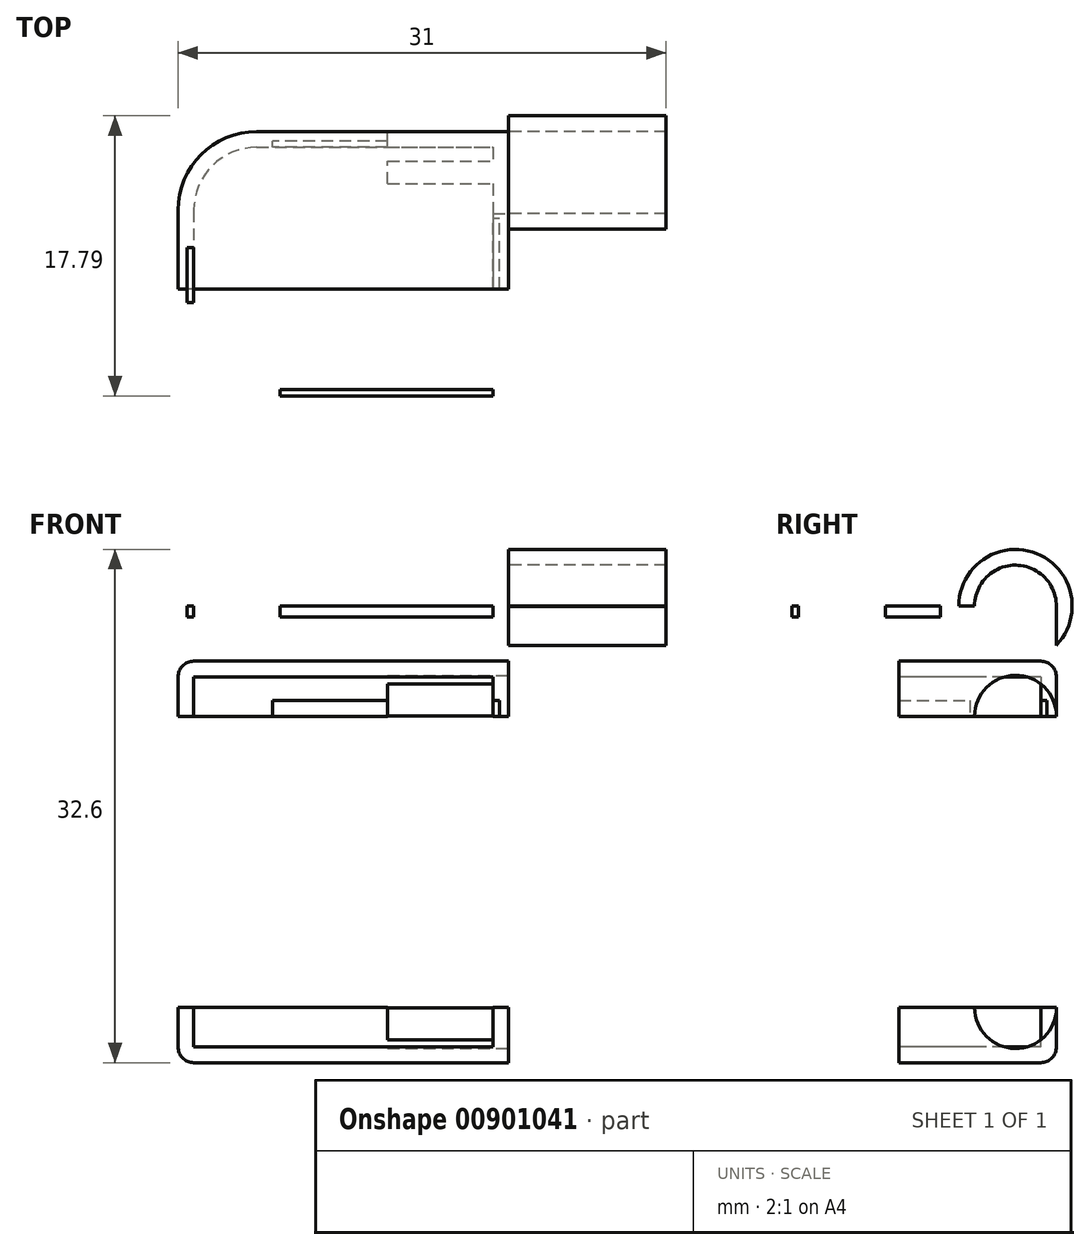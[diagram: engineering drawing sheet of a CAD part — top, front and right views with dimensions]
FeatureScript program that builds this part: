
annotation { "Feature Type Name" : "Feature", "Feature Type Description" : "" }
export const myFeature = defineFeature(function(context is Context, id is Id, definition is map)
    precondition{}
    {
        {
            var Q0;
            Q0=qCreatedBy(makeId("Top.planeOp"),FACE);
            var sketch = newSketch(context, id + "F0", { "sketchPlane" : qUnion([Q0])});
            skLineSegment(sketch, "E0.bottom", {"start": v(-4.03, 8.7) * mm, "end": v(11.97, 8.7) * mm});
            skLineSegment(sketch, "E0.top", {"start": v(-9.03, -1.3) * mm, "end": v(11.97, -1.3) * mm});
            skLineSegment(sketch, "E0.left", {"start": v(-9.03, 3.7) * mm, "end": v(-9.03, -1.3) * mm});
            skLineSegment(sketch, "E0.right", {"start": v(11.97, 8.7) * mm, "end": v(11.97, -1.3) * mm});
            skPoint(sketch, "E1.visualSharp", {"position": v(-9.03, 8.7) * mm});
            skArc(sketch, "E1.filletArc", {"start": v(-4.03, 8.7) * mm, "mid": v(-7.56, 7.23) * mm, "end": v(-9.03, 3.7) * mm});
            skSolve(sketch);
        }
        {
            var Q0;
            Q0=qSketchRegion(id+"F0",true);
            extrude(context, id + "F1", {"entities" : qUnion([Q0]), "depth" : 3.5 * mm, "offsetDistance" : 25 * mm});
        }
        {
            var Q0;
            Q0=makeQuery(id+"F1.opExtrude","CAP_FACE",FACE,{"disambiguationData":[OSD([sQuery(id+"F0.wireOp",EDGE,"E0.bottom"),sQuery(id+"F0.wireOp",EDGE,"E0.top"),sQuery(id+"F0.wireOp",EDGE,"E0.left"),sQuery(id+"F0.wireOp",EDGE,"E0.right"),sQuery(id+"F0.wireOp",EDGE,"E1.filletArc")])],"isStart":false});
            var sketch = newSketch(context, id + "F2", { "sketchPlane" : qUnion([Q0])});
            skLineSegment(sketch, "E2.0", {"start": v(-8.03, 3.7) * mm, "end": v(-8.03, -1.3) * mm});
            skArc(sketch, "E2.1", {"start": v(-4.03, 7.7) * mm, "mid": v(-6.86, 6.52) * mm, "end": v(-8.03, 3.7) * mm});
            skLineSegment(sketch, "E2.2", {"start": v(-4.03, 7.7) * mm, "end": v(10.97, 7.7) * mm});
            skLineSegment(sketch, "E2.3", {"start": v(10.97, 7.7) * mm, "end": v(10.97, -1.3) * mm});
            skSolve(sketch);
        }
        {
            var Q0;
            {var subQ1=sQuery(id+"F2.wireOp",EDGE,"E2.0");Q0=makeQuery(id+"F2.imprint","IMPRINT",FACE,{"disambiguationData":[TD([[makeQuery(id+"F2.imprint","IMPRINT",EDGE,{"derivedFrom":subQ1}),1.0]])]});}
            extrude(context, id + "F3", {"entities" : qUnion([Q0]), "operationType" : NewBodyOperationType.REMOVE, "oppositeDirection" : true, "depth" : 2.5 * mm, "offsetDistance" : 25 * mm});
        }
        {
            var Q0;
            Q0=makeQuery(id+"F1.opExtrude","CAP_EDGE",EDGE,{"disambiguationData":[OSD([sQuery(id+"F0.wireOp",EDGE,"E0.bottom")])],"isStart":true});
            var Q1;
            Q1=makeQuery(id+"F1.opExtrude","CAP_EDGE",EDGE,{"disambiguationData":[OSD([sQuery(id+"F0.wireOp",EDGE,"E1.filletArc")])],"isStart":true});
            var Q2;
            Q2=makeQuery(id+"F1.opExtrude","CAP_EDGE",EDGE,{"disambiguationData":[OSD([sQuery(id+"F0.wireOp",EDGE,"E0.left")])],"isStart":true});
            fillet(context, id + "F4", {"entities" : qUnion([Q0, Q1, Q2]), "radius" : 1 * mm, "tangentPropagation" : true, "allowEdgeOverflow" : false});
        }
        {
            var Q0;
            Q0=makeQuery(id+"F1.opExtrude","SWEPT_FACE",FACE,{"disambiguationData":[OSD([sQuery(id+"F0.wireOp",EDGE,"E0.right")])]});
            var sketch = newSketch(context, id + "F5", { "sketchPlane" : qUnion([Q0])});
            skCircle(sketch, "E3", {"center": v(6.1, 3.5) * mm, "radius": 2.6 * mm});
            skSolve(sketch);
        }
        {
            var Q0;
            Q0=qSketchRegion(id+"F5",true);
            extrude(context, id + "F6", {"entities" : qUnion([Q0]), "operationType" : NewBodyOperationType.REMOVE, "oppositeDirection" : true, "depth" : 7.7 * mm, "offsetDistance" : 25 * mm});
        }
        {
            var Q0;
            Q0=makeQuery(id+"F1.opExtrude","SWEPT_FACE",FACE,{"disambiguationData":[OSD([sQuery(id+"F0.wireOp",EDGE,"E0.right")])]});
            var sketch = newSketch(context, id + "F7", { "sketchPlane" : qUnion([Q0])});
            skCircle(sketch, "E4", {"center": v(6.1, 3.5) * mm, "radius": 2.6 * mm});
            skCircle(sketch, "E5", {"center": v(6.1, 3.5) * mm, "radius": 3.6 * mm});
            skSolve(sketch);
        }
        {
            var Q0;
            {var subQ0=sQuery(id+"F7.wireOp",EDGE,"E4");var subQ1=sQuery(id+"F0.wireOp",EDGE,"E0.bottom");var subQ2=sQuery(id+"F0.wireOp",EDGE,"E0.right");var subQ7=makeQuery(id+"F1.opExtrude","CAP_EDGE",EDGE,{"disambiguationData":[OSD([subQ2])],"isStart":false});var subQ8=makeQuery(id+"F6.boolean.opBoolean","SPLIT",EDGE,{"disambiguationData":[TD([makeQuery(id+"F1.opExtrude","SWEPT_FACE",FACE,{"disambiguationData":[OSD([subQ1])]})])],"derivedFrom":subQ7});var subQ9=makeQuery(id+"F7.imprint","INTERSECT",VERTEX,{"derivedFrom":[subQ8,subQ0]});Q0=makeQuery(id+"F7.imprint","IMPRINT",FACE,{"disambiguationData":[TD([[makeQuery(id+"F7.imprint","IMPRINT",EDGE,{"disambiguationData":[TD([[subQ9,1.0]])],"derivedFrom":subQ0}),-1.0]])]});}
            extrude(context, id + "F8", {"entities" : qUnion([Q0]), "operationType" : NewBodyOperationType.ADD, "depth" : 10 * mm, "offsetDistance" : 25 * mm});
        }
        {
            var Q0;
            Q0=makeQuery(id+"F1.opExtrude","SWEPT_BODY",BODY,{"disambiguationData":[OSD([sQuery(id+"F0.wireOp",EDGE,"E0.bottom"),sQuery(id+"F0.wireOp",EDGE,"E0.top"),sQuery(id+"F0.wireOp",EDGE,"E0.left"),sQuery(id+"F0.wireOp",EDGE,"E0.right"),sQuery(id+"F0.wireOp",EDGE,"E1.filletArc")])]});
            var Q1;
            Q1=makeQuery(id+"F1.opExtrude","CAP_FACE",FACE,{"disambiguationData":[OSD([sQuery(id+"F0.wireOp",EDGE,"E0.bottom"),sQuery(id+"F0.wireOp",EDGE,"E0.top"),sQuery(id+"F0.wireOp",EDGE,"E0.left"),sQuery(id+"F0.wireOp",EDGE,"E0.right"),sQuery(id+"F0.wireOp",EDGE,"E1.filletArc")])],"isStart":true});
            mirror(context, id + "F9", {"entities" : qUnion([Q0]), "mirrorPlane" : qUnion([Q1])});
        }
        {
            var Q0;
            Q0=makeQuery(id+"F1.opExtrude","SWEPT_BODY",BODY,{"disambiguationData":[OSD([sQuery(id+"F0.wireOp",EDGE,"E0.bottom"),sQuery(id+"F0.wireOp",EDGE,"E0.top"),sQuery(id+"F0.wireOp",EDGE,"E0.left"),sQuery(id+"F0.wireOp",EDGE,"E0.right"),sQuery(id+"F0.wireOp",EDGE,"E1.filletArc")])]});
            var Q1;
            Q1=makeQuery(id+"F1.opExtrude","SWEPT_EDGE",EDGE,{"disambiguationData":[OSD([sQuery(id+"F0.wireOp",EDGE,"E0.top"),sQuery(id+"F0.wireOp",EDGE,"E0.right")])]});
            var Q2;
            Q2=makeQuery(id+"F1.opExtrude","SWEPT_EDGE",EDGE,{"disambiguationData":[OSD([sQuery(id+"F0.wireOp",EDGE,"E0.top"),sQuery(id+"F0.wireOp",EDGE,"E0.right")])]});
            transform(context, id + "F10", {"entities" : qUnion([Q0]), "transformType" : TransformType.TRANSLATION_DISTANCE, "transformDirection" : qUnion([Q2]), "distance" : 17.8 * mm, "oppositeDirection" : true, "makeCopy" : false});
        }
        {
            var Q0;
            {var subQ0=sQuery(id+"F0.wireOp",EDGE,"E0.bottom");var subQ1=makeQuery(id+"F1.opExtrude","SWEPT_FACE",FACE,{"disambiguationData":[OSD([subQ0])]});var subQ2=sQuery(id+"F0.wireOp",EDGE,"E0.right");var subQ3=makeQuery(id+"F1.opExtrude","SWEPT_FACE",FACE,{"disambiguationData":[OSD([subQ2])]});var subQ4=sQuery(id+"F0.wireOp",EDGE,"E1.filletArc");var subQ5=sQuery(id+"F0.wireOp",EDGE,"E0.left");var subQ6=sQuery(id+"F0.wireOp",EDGE,"E0.top");var subQ7=makeQuery(id+"F1.opExtrude","CAP_FACE",FACE,{"disambiguationData":[OSD([subQ0,subQ6,subQ5,subQ2,subQ4])],"isStart":false});var subQ8=makeQuery(id+"F6.opExtrude","SWEPT_FACE",FACE,{"disambiguationData":[OSD([sQuery(id+"F5.wireOp",EDGE,"E3")])]});var subQ9=makeQuery(id+"F6.boolean.opBoolean","SPLIT",EDGE,{"disambiguationData":[TD([subQ1])],"derivedFrom":makeQuery(id+"F1.opExtrude","CAP_EDGE",EDGE,{"disambiguationData":[OSD([subQ2])],"isStart":false})});Q0=makeQuery(id+"F9.opPattern","COPY",FACE,{"derivedFrom":makeQuery(id+"F8.boolean.opBoolean","MERGE",FACE,{"derivedFrom":[makeQuery(id+"F6.boolean.opBoolean","SPLIT",FACE,{"disambiguationData":[TD([subQ1,makeQuery(id+"F1.opExtrude","SWEPT_FACE",FACE,{"disambiguationData":[OSD([subQ6])]}),makeQuery(id+"F1.opExtrude","SWEPT_FACE",FACE,{"disambiguationData":[OSD([subQ5])]}),subQ3,makeQuery(id+"F1.opExtrude","SWEPT_FACE",FACE,{"disambiguationData":[OSD([subQ4])]}),makeQuery(id+"F3.boolean.opBoolean","COPY",FACE,{"derivedFrom":makeQuery(id+"F3.opExtrude","SWEPT_FACE",FACE,{"disambiguationData":[OSD([sQuery(id+"F2.wireOp",EDGE,"E2.0")])]})}),makeQuery(id+"F3.boolean.opBoolean","COPY",FACE,{"derivedFrom":makeQuery(id+"F3.opExtrude","SWEPT_FACE",FACE,{"disambiguationData":[OSD([sQuery(id+"F2.wireOp",EDGE,"E2.1")])]})}),makeQuery(id+"F3.boolean.opBoolean","COPY",FACE,{"derivedFrom":makeQuery(id+"F3.opExtrude","SWEPT_FACE",FACE,{"disambiguationData":[OSD([sQuery(id+"F2.wireOp",EDGE,"E2.2")])]})}),makeQuery(id+"F3.boolean.opBoolean","COPY",FACE,{"derivedFrom":makeQuery(id+"F3.opExtrude","SWEPT_FACE",FACE,{"disambiguationData":[OSD([sQuery(id+"F2.wireOp",EDGE,"E2.3")])]})}),subQ8])],"derivedFrom":subQ7}),makeQuery(id+"F8.opExtrude","SWEPT_FACE",FACE,{"disambiguationData":[OSD([subQ2]),TDD([makeQuery(id+"F7.imprint","IMPRINT",EDGE,{"disambiguationData":[TD([[makeQuery(id+"F7.imprint","INTERSECT",VERTEX,{"derivedFrom":[subQ9,sQuery(id+"F7.wireOp",EDGE,"E4")]}),1.0]])],"derivedFrom":subQ9})])]})]}),"instanceName":"1"});}
            var sketch = newSketch(context, id + "F11", { "sketchPlane" : qUnion([Q0])});
            skLineSegment(sketch, "E6.bottom", {"start": v(10.97, -7.7) * mm, "end": v(-3.03, -7.7) * mm});
            skLineSegment(sketch, "E6.top", {"start": v(10.97, -8.1) * mm, "end": v(-3.03, -8.1) * mm});
            skLineSegment(sketch, "E6.left", {"start": v(10.97, -7.7) * mm, "end": v(10.97, -8.1) * mm});
            skLineSegment(sketch, "E6.right", {"start": v(-3.03, -7.7) * mm, "end": v(-3.03, -8.1) * mm});
            skLineSegment(sketch, "E7.bottom", {"start": v(10.97, 1.3) * mm, "end": v(11.37, 1.3) * mm});
            skLineSegment(sketch, "E7.top", {"start": v(10.97, -3.2) * mm, "end": v(11.37, -3.2) * mm});
            skLineSegment(sketch, "E7.left", {"start": v(10.97, 1.3) * mm, "end": v(10.97, -3.2) * mm});
            skLineSegment(sketch, "E7.right", {"start": v(11.37, 1.3) * mm, "end": v(11.37, -3.2) * mm});
            skSolve(sketch);
        }
        {
            var Q0;
            Q0 = qSketchRegion(id + "F11", true);
            extrude(context, id + "F12", {"entities" : qUnion([Q0]), "operationType" : NewBodyOperationType.REMOVE, "oppositeDirection" : true, "depth" : 1 * mm, "offsetDistance" : 25 * mm});
        }
        {
            var Q0;
            {var subQ0=sQuery(id+"F0.wireOp",EDGE,"E0.bottom");var subQ1=makeQuery(id+"F1.opExtrude","SWEPT_FACE",FACE,{"disambiguationData":[OSD([subQ0])]});var subQ2=sQuery(id+"F0.wireOp",EDGE,"E0.right");var subQ3=makeQuery(id+"F1.opExtrude","SWEPT_FACE",FACE,{"disambiguationData":[OSD([subQ2])]});var subQ4=sQuery(id+"F0.wireOp",EDGE,"E1.filletArc");var subQ5=sQuery(id+"F0.wireOp",EDGE,"E0.left");var subQ6=sQuery(id+"F0.wireOp",EDGE,"E0.top");var subQ7=makeQuery(id+"F1.opExtrude","CAP_FACE",FACE,{"disambiguationData":[OSD([subQ0,subQ6,subQ5,subQ2,subQ4])],"isStart":false});var subQ8=makeQuery(id+"F6.opExtrude","SWEPT_FACE",FACE,{"disambiguationData":[OSD([sQuery(id+"F5.wireOp",EDGE,"E3")])]});var subQ9=makeQuery(id+"F6.boolean.opBoolean","SPLIT",EDGE,{"disambiguationData":[TD([subQ1])],"derivedFrom":makeQuery(id+"F1.opExtrude","CAP_EDGE",EDGE,{"disambiguationData":[OSD([subQ2])],"isStart":false})});Q0=makeQuery(id+"F8.boolean.opBoolean","MERGE",FACE,{"derivedFrom":[makeQuery(id+"F6.boolean.opBoolean","SPLIT",FACE,{"disambiguationData":[TD([subQ1,makeQuery(id+"F1.opExtrude","SWEPT_FACE",FACE,{"disambiguationData":[OSD([subQ6])]}),makeQuery(id+"F1.opExtrude","SWEPT_FACE",FACE,{"disambiguationData":[OSD([subQ5])]}),subQ3,makeQuery(id+"F1.opExtrude","SWEPT_FACE",FACE,{"disambiguationData":[OSD([subQ4])]}),makeQuery(id+"F3.boolean.opBoolean","COPY",FACE,{"derivedFrom":makeQuery(id+"F3.opExtrude","SWEPT_FACE",FACE,{"disambiguationData":[OSD([sQuery(id+"F2.wireOp",EDGE,"E2.0")])]})}),makeQuery(id+"F3.boolean.opBoolean","COPY",FACE,{"derivedFrom":makeQuery(id+"F3.opExtrude","SWEPT_FACE",FACE,{"disambiguationData":[OSD([sQuery(id+"F2.wireOp",EDGE,"E2.1")])]})}),makeQuery(id+"F3.boolean.opBoolean","COPY",FACE,{"derivedFrom":makeQuery(id+"F3.opExtrude","SWEPT_FACE",FACE,{"disambiguationData":[OSD([sQuery(id+"F2.wireOp",EDGE,"E2.2")])]})}),makeQuery(id+"F3.boolean.opBoolean","COPY",FACE,{"derivedFrom":makeQuery(id+"F3.opExtrude","SWEPT_FACE",FACE,{"disambiguationData":[OSD([sQuery(id+"F2.wireOp",EDGE,"E2.3")])]})}),subQ8])],"derivedFrom":subQ7}),makeQuery(id+"F8.opExtrude","SWEPT_FACE",FACE,{"disambiguationData":[OSD([subQ2]),TDD([makeQuery(id+"F7.imprint","IMPRINT",EDGE,{"disambiguationData":[TD([[makeQuery(id+"F7.imprint","INTERSECT",VERTEX,{"derivedFrom":[subQ9,sQuery(id+"F7.wireOp",EDGE,"E4")]}),1.0]])],"derivedFrom":subQ9})])]})]});}
            var sketch = newSketch(context, id + "F13", { "sketchPlane" : qUnion([Q0])});
            skLineSegment(sketch, "E8.bottom", {"start": v(10.97, 7.7) * mm, "end": v(-2.54, 7.7) * mm});
            skLineSegment(sketch, "E8.top", {"start": v(10.97, 8.1) * mm, "end": v(-2.54, 8.1) * mm});
            skLineSegment(sketch, "E8.left", {"start": v(10.97, 7.7) * mm, "end": v(10.97, 8.1) * mm});
            skLineSegment(sketch, "E8.right", {"start": v(-2.54, 7.7) * mm, "end": v(-2.54, 8.1) * mm});
            skLineSegment(sketch, "E9.bottom", {"start": v(-8.47, 2.17) * mm, "end": v(-8.03, 2.17) * mm});
            skLineSegment(sketch, "E9.top", {"start": v(-8.47, -1.3) * mm, "end": v(-8.03, -1.3) * mm});
            skLineSegment(sketch, "E9.left", {"start": v(-8.47, 2.17) * mm, "end": v(-8.47, -1.3) * mm});
            skLineSegment(sketch, "E9.right", {"start": v(-8.03, 2.17) * mm, "end": v(-8.03, -1.3) * mm});
            skSolve(sketch);
        }
        {
            var Q0;
            Q0 = qSketchRegion(id + "F13", true);
            extrude(context, id + "F14", {"entities" : qUnion([Q0]), "operationType" : NewBodyOperationType.ADD, "depth" : 0.7 * mm, "offsetDistance" : 25 * mm});
        }
        {
            var Q0;
            Q0=makeQuery(id+"F1.opExtrude","SWEPT_BODY",BODY,{"disambiguationData":[OSD([sQuery(id+"F0.wireOp",EDGE,"E0.bottom"),sQuery(id+"F0.wireOp",EDGE,"E0.top"),sQuery(id+"F0.wireOp",EDGE,"E0.left"),sQuery(id+"F0.wireOp",EDGE,"E0.right"),sQuery(id+"F0.wireOp",EDGE,"E1.filletArc")])]});
            transform(context, id + "F15", {"entities" : qUnion([Q0]), "transformType" : TransformType.TRANSLATION_3D, "dx" : 0 * mm, "dy" : 0 * mm, "dz" : -43.3 * mm, "makeCopy" : false});
        }
    });
